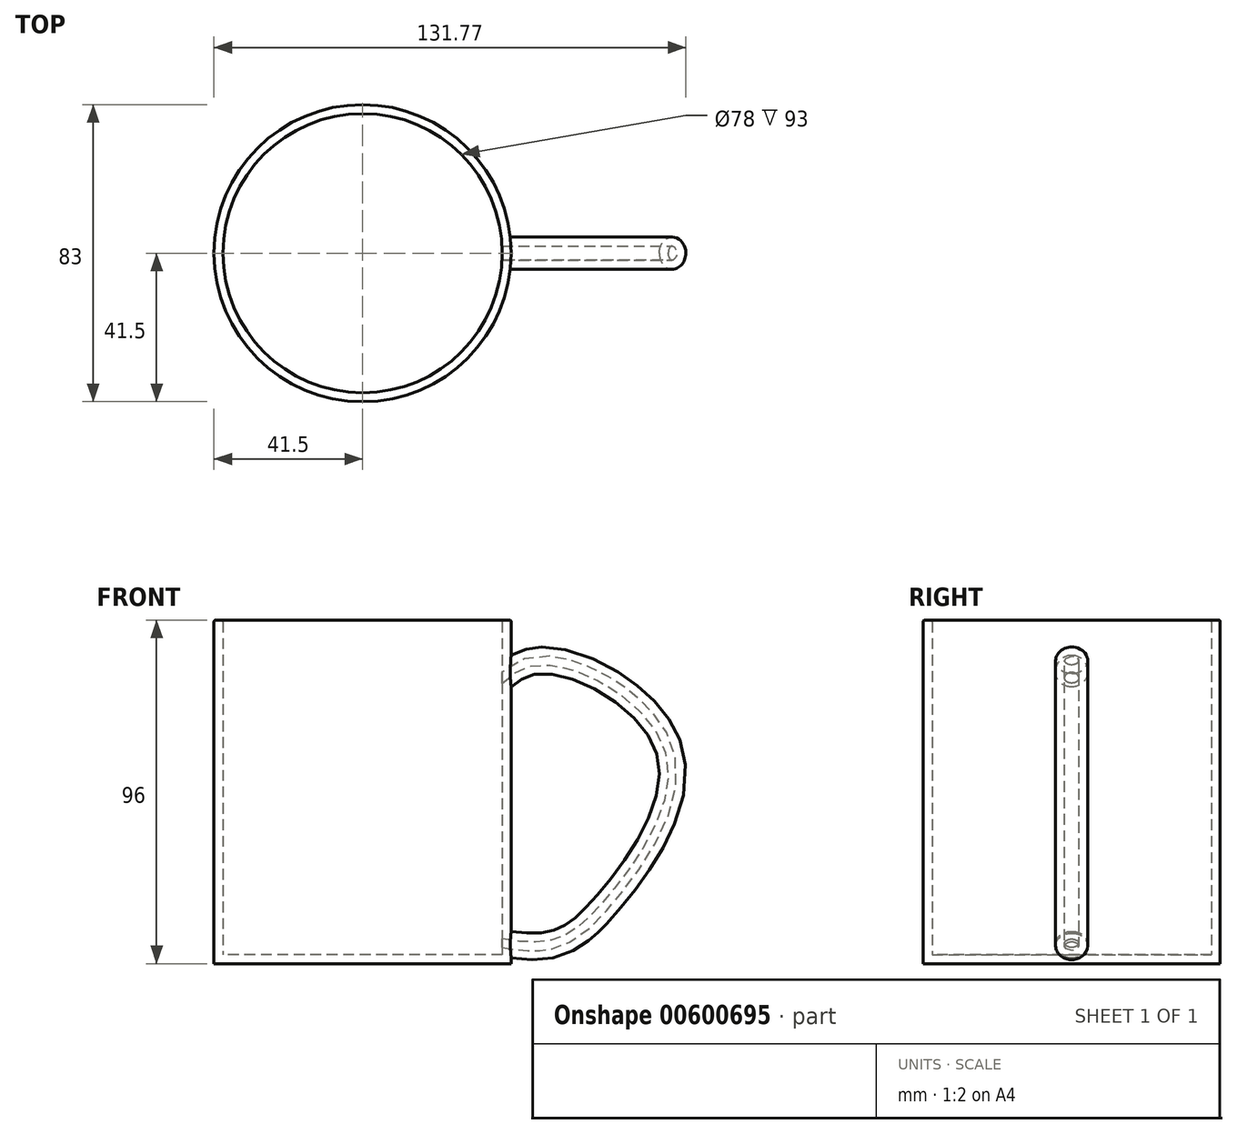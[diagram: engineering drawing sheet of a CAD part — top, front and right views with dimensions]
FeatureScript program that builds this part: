
annotation { "Feature Type Name" : "Feature", "Feature Type Description" : "" }
export const myFeature = defineFeature(function(context is Context, id is Id, definition is map)
    precondition{}
    {
        {
            var Q0;
            Q0=qCreatedBy(makeId("Top.planeOp"),FACE);
            var sketch = newSketch(context, id + "F0", { "sketchPlane" : qUnion([Q0])});
            skCircle(sketch, "E0", {"center": v(0, 0) * mm, "radius": 41.5 * mm});
            skSolve(sketch);
        }
        {
            var Q0;
            Q0 = qSketchRegion(id + "F0", true);
            extrude(context, id + "F1", {"entities" : qUnion([Q0]), "depth" : 96 * mm, "offsetDistance" : 25 * mm});
        }
        {
            var Q0;
            Q0=qCreatedBy(makeId("Front.planeOp"),FACE);
            var sketch = newSketch(context, id + "F2", { "sketchPlane" : qUnion([Q0])});
            skFitSpline(sketch, "E1", {"points": [v(34.68, 74.2) * mm, v(50.84, 83.83) * mm, v(84.8, 59.4) * mm, v(69.44, 19.34) * mm, v(52.68, 6.26) * mm, v(33.59, 7.52) * mm], "startDerivative": vector(78.15, 88.19) * mm, "endDerivative": vector(-121.27, 23.59) * mm});
            skSolve(sketch);
        }
        {
            var Q0;
            Q0=qCreatedBy(makeId("Right.planeOp"),FACE);
            cPlane(context, id + "F3", {"entities" : qUnion([Q0]), "cplaneType" : CPlaneType.OFFSET, "offset" : 41.5 * mm, "width" : 150 * mm, "height" : 150 * mm});
        }
        {
            var Q0;
            Q0=qCreatedBy(id+"F3.planeOp",FACE);
            var sketch = newSketch(context, id + "F4", { "sketchPlane" : qUnion([Q0])});
            skCircle(sketch, "E2", {"center": v(0, 81.77) * mm, "radius": 4.48 * mm});
            skSolve(sketch);
        }
        {
            var Q0;
            Q0=makeQuery(id+"F4.imprint","IMPRINT",FACE,{"disambiguationData":[TD([[makeQuery(id+"F4.imprint","IMPRINT",EDGE,{"derivedFrom":sQuery(id+"F4.wireOp",EDGE,"E2")}),1.0]])]});
            var Q1;
            Q1=sQuery(id+"F2.wireOp",EDGE,"d4d2a5f8-eda8-4499-8d14-32bffd675819");
            var Q2;
            Q2=sQuery(id+"F2.wireOp",EDGE,"E1");
            sweep(context, id + "F5", {"operationType" : NewBodyOperationType.ADD, "profiles" : qUnion([Q0]), "path" : qUnion([Q1, Q2])});
        }
        {
            var Q0;
            Q0=makeQuery(id+"F1.opExtrude","CAP_FACE",FACE,{"disambiguationData":[OSD([sQuery(id+"F0.wireOp",EDGE,"E0")])],"isStart":false});
            shell(context, id + "F6", {"entities" : qUnion([Q0]), "thickness" : 2.5 * mm});
        }
        {
            var Q0;
            Q0=makeQuery(id+"F1.opExtrude","CAP_EDGE",EDGE,{"disambiguationData":[OSD([sQuery(id+"F0.wireOp",EDGE,"E0")])],"isStart":false});
            var Q1;
            {var subQ0=sQuery(id+"F0.wireOp",EDGE,"E0");Q1=makeQuery(id+"F6.opShell","OFFSET_EDGE",EDGE,{"disambiguationData":[OSD([subQ0]),TDD([makeQuery(id+"F1.opExtrude","CAP_EDGE",EDGE,{"disambiguationData":[OSD([subQ0])],"isStart":false})])]});}
            fillet(context, id + "F7", {"entities" : qUnion([Q0, Q1]), "radius" : 0.5 * mm, "tangentPropagation" : true, "allowEdgeOverflow" : false});
        }
    });
